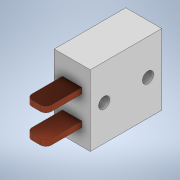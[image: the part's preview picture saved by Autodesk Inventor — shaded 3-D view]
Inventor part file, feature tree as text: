
AUTODESK INVENTOR PART (.ipt)
format: ipt  version: 2020 (Build 240168000, 168)  size: 137,216 bytes
history: native  units: in
note: dims shown in document units (in); Inventor stores cm internally (conversion verified against a paired STEP export)
features: extrude x2, sketch x2, fillet x1
ambient origin geometry x8: Origin, YZ Plane, XZ Plane, XY Plane, X Axis, Y Axis, Z Axis, Center Point
bodies: Solid1 (feature_tree)
feature tree (5):
  extrude  "Extrusion1"  Depth=0.5079in
  extrude  "Extrusion2"  Depth=0.0394in
  fillet  "Fillet1"  Radius=0.0787in
  sketch  "Sketch1"  dims[d0=0.502in d1=0.5079in]
  sketch  "Sketch2"  dims[d2=0.0787in d3=0.0984in d4=0.0787in d5=0.0984in d6=0.2559in d7=0.0in d8=0.1378in d9=0.0394in d12=0.1378in d13=0.1378in d14=0.2559in d15=0.0in d16=0.0394in]
